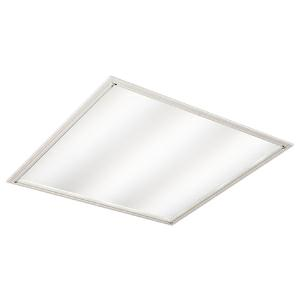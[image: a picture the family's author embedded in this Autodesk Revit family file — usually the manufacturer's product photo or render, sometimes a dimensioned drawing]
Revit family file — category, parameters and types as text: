
# Revit family: 3f_filippi_-_l_320_lgs_3f_filippi_-_21580_-_l_323x10w_led_lgs_596x596
name_source: partatom
category: Lighting Fixtures
units: mm (PartAtom-declared; Revit-internal decimal feet)

## family parameters
Cut with Voids When Loaded = No
Host = Face
Light Source = No
Part Type = Normal
Room Calculation Point = No
Round Connector Dimension = Use Diameter
Shared = No

## types (1)
- 3F Filippi - L 320 LGS (1 x LED, 3178 lm, 34 W, 4000 K)
    Apparent Load = 34 VA
    Approval mark = ENEC
    CIE Flux Codes = 64 89 98 100 100
    Color Rendering = 80
    Color Temperature = 4000 K
    Control Gear = Electronic ballast
    Default Elevation = 1800 mm
    Description = ILLUMINOTECHNICAL
Luminous efficiency 100% (DLOR 100%, ULOR 0%).
Initial luminous flux of the luminaire 3178 lm.
Direct symmetric distribution.
Installation Interdistance Transv.D = 1.17 x hu - Long.D = 1.16 x hu.
Average luminance <1500 cd/m² for radial angles >65°.
Tabular UGR (CIE 117 - 4H-8H; S=0.25H; 70/50/20): RUG 17.2 - 17.2.
Beam angle: 85° - 84°.
Luminous efficacy 93 lm/W.
Lifetime (L93/B10): 30000 h. (tq+25°C)
Lifetime (L90/B10): 50000 h. (tq+25°C)
Lifetime (L85/B10): 80000 h. (tq+25°C)
Lifetime (L80/B10): 100000 h. (tq+25°C)
Sudden decreased luminous flux after 50000 hours: 0% (C0).
Photobiological safety in compliance with IEC/TR 62778: RG0 risk exempt, (IEC 62471).
In compliance with IEC/EN 62722-2-1 - IEC/EN 62717 standards.

SOURCE
3 linear LED modules 10W/840.
Energy efficiency class (UE 2019/2020 - UE 2019/2015): D.
CIE 13.3 Colour rendering index: CRI >80 (R9 <50%).
IES TM-30 Fidelity Index: Rf = 84 Rg = 95.
CCT nominal colour temperature 4000 K.
Colour initial tolerance (MacAdam): SDCM 2.

MECHANICAL
Housing in hot-galvanised steel, painted in white polyester.
Micro-prismatic flat diffuser in transparent methacrylate (PMMA), multilenticular exterior, anti-glare, locked to the white painted aluminium perimetral frame, sealing gasket, hinged opening.
Anti-glare opal polycarbonate filter for brightness uniformity.
Luminaire with limited surface temperature. - D - (EN 60598-2-24)
Dimensions: 596x596 mm, height 80 mm. Weight 4.69 kg.
IP54 protection degree for exposed part, IP20 for recessed part.
Mechanical strength to impacts IK06 (1 joule).
Glow-wire test resistance 650°C.

ELECTRICAL
Halogen Free electronic wiring 230V-50/60Hz, power factor 0.90, THD <25%, constant output current, SELV, class I, 1 driver.
Power of the luminaire 34 W.
CE - IEC 60598-1 - EN 60598-1.
SAFE FLICKER: PstLM=<1 and SVM=<0.4 (IEC TR 61547-1 and IEC TR 63158), to ensure a more comfortable and safe light.
Luminaire compliant with EN 60598-2-22 for power supply from a centralised emergency system CPSS (Central Power Supply System), not incorporated in the luminaire - high risk areas excluded. The default power and flux are 100% in AC and 100% in DC.
Ambient temperature from 0°C to +25°C.
Temperature class T6 max 85°C.
Relative humidity UR: <85%.

INSTALLATION
Lay-in recessed fitting.
On request: pull-up recessed fitting with brackets.
False ceiling carving: 580x580 mm.
All accessories dedicated to this product are available on the Catalog and on our website www.3F-Filippi.com.

APPLICATIONS
Environments: sterilized, aseptic.
In environments with VDU's, managerial offices and staterooms, environments involving accurate visual tasks where a diffused and soft light for an optimum visual comfort and the source total shielding are required.

WARNING
Luminaire designed for disposal/recycling at end-of-life.
Replaceable (LED only) light source by a professional. Replaceable control gear by a professional.
    Height = 0 mm  [stored 0 ft]
    Lamp = 1 x LED
    Lamp Light Flux = 3178 lm
    Lamp Power = 34 W
    Lamp count = 1
    Length = 596 mm
    Lifetime = 50000 h
    Luminous efficacy = 93 lm/W
    Manufacturer = 3F Filippi
    ModVariant = No
    Model = 3F Filippi - 21580 - L 323x10W LED LGS 596x596
    Mounting Place = Ceiling
    Mounting Type = Recessed
    Number of Poles = 1
    OnlyDefault = Yes
    Power Factor = 1
    Product Name = 3F Filippi - L 320 LGS
    Product group = recessed luminaire
    ProductGroupID = 4
    Protection Class = Protection class I
    Protection Degree = IP 20
    RLX_Detail_Level = 1
    RLX_Emergency_Light_Flux = 0 lm
    RLX_Emergency_Type = 0
    RLX_Emergency_Type_DB = No
    RlxData = <blob elided: 33989 chars, md5=1646ff1c>
    Socket = socket
    Standby Power = 0 W
    System Light Flux = 3178 lm
    System Power = 34 W
    Type Comments = Product without accessories
    Type Image = 3ffilippi_l_320_led_lgs.jpg
    URL = http://relux.com
    VarID = ---
    Voltage = 0 V
    Weight = 0.00 kg
    Width = 596 mm

note: [stored X ft] marks values corroborated as IEEE doubles in the binary element streams (Revit-internal decimal feet)

## geometry (parser evidence)
native form markers: Blend x4, Sweep x8
no freeform markers — native parametric forms only
